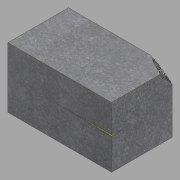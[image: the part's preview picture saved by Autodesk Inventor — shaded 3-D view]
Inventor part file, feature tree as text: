
AUTODESK INVENTOR PART (.ipt)
format: ipt  version: 2022.1 (Build 261234020, 234B)  size: 514,048 bytes
history: native  units: in
note: dims shown in document units (in); Inventor stores cm internally (conversion verified against a paired STEP export)
features: sketch x12, extrude x6, plane x4, loft x2
ambient origin geometry x8: Origin, YZ Plane, XZ Plane, XY Plane, X Axis, Y Axis, Z Axis, Center Point
bodies: Solid1 (feature_tree)
feature tree (24):
  extrude  "Extrusion1"  Depth=60.0in
  loft  "Loft1"
  sketch  "Sketch7"  dims[d79=0.0in d80=90.0deg d81=0.0in d82=0.0in]
  sketch  "Sketch8"  dims[d83=0.0in d84=0.0in d85=97.795in d86=0.0in]
  loft  "Loft2"
  sketch  "Sketch10"
  plane  "Work Plane1"
  plane  "Work Plane3"
  extrude  "Extrusion2"  TaperAngle=0.0deg  [1 undecoded]
  plane  "Work Plane4"
  extrude  "Extrusion3"  Depth=97.795in TaperAngle=0.0deg
  plane  "Work Plane5"
  extrude  "Extrusion4"  Depth=1.5in
  extrude  "Extrusion5"  [1 undecoded]
  extrude  "Extrusion6"  [1 undecoded]
  sketch  "Sketch1"  dims[d0=60.0in d1=35.0in]
  sketch  "Sketch5"  dims[d2=35.0in d3=0.0in d73=0.0in d74=90.0deg]
  sketch  "Sketch6"  dims[d75=0.0in d76=90.0deg d77=0.0in d78=90.0deg]
  sketch  "Sketch9"  dims[d87=0.25in d88=-0.2749in d89=1.5in d90=-0.0344in]
  sketch  "Sketch11"
  sketch  "Sketch12"
  sketch  "Sketch13"
  sketch  "Sketch14"
  sketch  "Sketch15"
note: 3 required parameter values undecoded (feature->parameter linkage not recoverable at this tier; creation-order binding heuristic only, values carry confidence <= 0.55)
